# Revit family: NBS_Allermuir_OffcChrs_Famiglia-en-us_LoungeChair
name_source: partatom
category: Furniture
revit_build: Autodesk Revit 2016 (Build: 20151007_0715(x64)
units: mm (PartAtom-declared; Revit-internal decimal feet)

## family parameters
Always vertical = Yes
Cut with Voids When Loaded = No
Room Calculation Point = No
Shared = No
Work Plane-Based = No

## types (3) — shared parameters
AssetType = Moveable
Category = Pr_40_50_12_57:Office chairs
CodePerformance = ANSI/BIFMA X5.1: 2011
DurationUnit = year
EnvironmentalProductDeclaration = http://www.thesenatorgroup.com
ExpectedLife = 10
Features = Molded foam construction, fully upholstered, solid ash frame with a clear finish, solid ash frame can be stained or color washed
IfcExportAs = IfcFurnitureType
IfcExportType = CHAIR
IsBuiltIn = No
ManufacturerName = Allermuir
ManufacturerURL = http://www.thesenatorgroup.com
ModelReference = Famiglia lounge
NBSCertification = www.nationalbimlibrary.com/cert/2tnqn1ct
NBSDescription = Office chairs
NBSReference = 45-35-20/330
OmniClassCode = 22-12 52 23
OmniClassTitle = Office Seating
OmniClassVersion = Table 22 2012-05-16
ProductInformation = http://www.thesenatorgroup.com
SeatBaseMaterial = NBS_Concept
SeatingHeight = 15 "
SeatingSeatMaterial = NBS_Concept
SeatsAndBacksFinish = Fully upholstered
SeatsAndBacksFinishOptions = Decorative railroad stitch detail to perimeter seam, two-tone upholstery
SeatsAndBacksMaterial = Molded foam
Status = UNSET
Uniclass2015Code = Pr_40_50_12_57
Uniclass2015Title = Office chairs
Uniclass2015Version = Products v1.9
Version = 1
WarrantyDescription = Allermuir warrant that its manufactured products are free from manufacturing defects in materials or workmanship for a period of ten years
WarrantyDurationParts = 10
WarrantyDurationUnit = year
zero-valued in all types: HighestSeatingHeight, LowestSeatingHeight

## per-type parameters (varying)
| type | BIMObjectName | Description | FrameColour | FrameColourOptions | FrameFinish | FrameMaterials | IntegralAccessories | Name | NominalDepth | NominalHeight | NominalLength | NominalWidth | OfficeChairBase | SeatsAndBacksColourOptions | Size | StandardsDurability | StandardsSafetyRequirements |
| FMG403 | NBS_Allermuir_OfficeChairs_Famiglia_FMG403-US | Lounge chair with wood frame |  | Stained, colour washed | Clear | Solid ash |  | OfficeChairs_Famiglia_FMG403-US_Allermuir | 34 " | 42 " | 33 " | 34 " | NBS_Allermuir_OffcChrs_Famiglia_WoodFrame | Black, White, Red, Light Grey, Dark Grey, Cream | 33 x 34.25 x 42.25" | ANSI/BIFMA X5.1: 2011 | ANSI/BIFMA X5.1: 2011 |
| FMG405 | NBS_Allermuir_OfficeChairs_Famiglia_FMG405-US | Lounge chair on a 4 star swivel base | Slate grey |  | Powder coat | Steel | Plastic glides | OfficeChairs_Famiglia_FMG405-US_Allermuir | 36 " | 42 " | 36 " | 36 " | NBS_Allermuir_OffcChrs_Famiglia_4StarSwivelBase | Black, White, Red, Light Grey, Dark Grey, Cream | 35.75 x 35.5 x 42.25" |  |  |
| FMG408 | NBS_Allermuir_OfficeChairs_Famiglia_FMG408-US | Lounge chair on wire frame |  | Chrome,  slate grey | Polished Chrome | Tubular steel | Plastic glides | OfficeChairs_Famiglia_FMG408-US_Allermuir | 34 " | 43 " | 33 " | 34 " | NBS_Allermuir_OffcChrs_Famiglia_WireFrame | Black, White, Red, Light Grey, Dark Grey, and Cream | 33 x 34.25 x 42.5" | ANSI/BIFMA X5.1: 2011 | ANSI/BIFMA X5.1: 2011 |

note: column(s) folded — value = type name in every type: ModelNumber

## geometry (parser evidence)
native form markers: Sweep x14
no freeform markers — native parametric forms only
